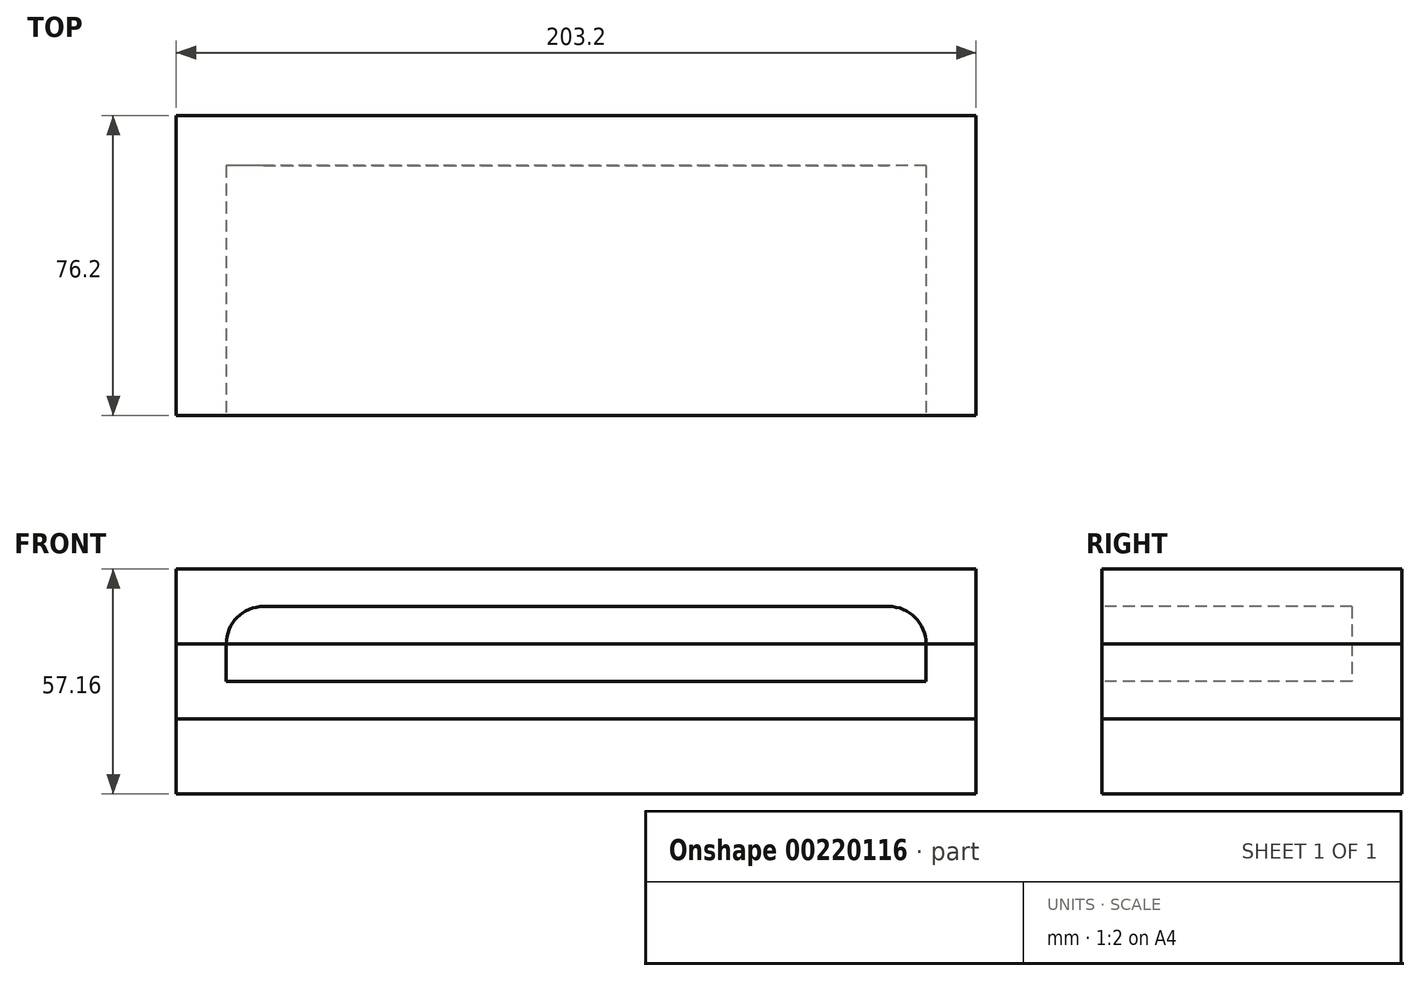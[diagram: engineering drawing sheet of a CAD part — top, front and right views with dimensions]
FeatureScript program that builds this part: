
annotation { "Feature Type Name" : "Feature", "Feature Type Description" : "" }
export const myFeature = defineFeature(function(context is Context, id is Id, definition is map)
    precondition{}
    {
        {
            assignVariable(context, id + "F0", {"name" : "d", "anyValue" : 76.2 * mm});
        }
        {
            assignVariable(context, id + "F1", {"name" : "top_th", "anyValue" : 3 / 101.6 * mm});
        }
        {
            assignVariable(context, id + "F2", {"name" : "bot_th", "anyValue" : getVariable(context, 'top_th')});
        }
        {
            assignVariable(context, id + "F3", {"name" : "slit_d", "anyValue" : 63.5 * mm});
        }
        {
            assignVariable(context, id + "F4", {"name" : "chamfer_angle", "anyValue" : 7});
        }
        {
            var Q0;
            Q0=qCreatedBy(makeId("Front.planeOp"),FACE);
            var sketch = newSketch(context, id + "F5", { "sketchPlane" : qUnion([Q0])});
            skLineSegment(sketch, "E0.bottom", {"start": v(-101.6, 9.52) * mm, "end": v(101.6, 9.52) * mm});
            skLineSegment(sketch, "E0.top", {"start": v(-101.6, -9.53) * mm, "end": v(101.6, -9.53) * mm});
            skLineSegment(sketch, "E0.left", {"start": v(-101.6, 9.52) * mm, "end": v(-101.6, -9.53) * mm});
            skLineSegment(sketch, "E0.right", {"start": v(101.6, 9.52) * mm, "end": v(101.6, -9.53) * mm});
            skSolve(sketch);
        }
        {
            var Q0;
            Q0=makeQuery(id+"F5.imprint","IMPRINT",FACE,{"disambiguationData":[TD([[makeQuery(id+"F5.imprint","IMPRINT",EDGE,{"derivedFrom":sQuery(id+"F5.wireOp",EDGE,"E0.bottom")}),-1.0]])]});
            var sketch = newSketch(context, id + "F6", { "sketchPlane" : qUnion([Q0])});
            skLineSegment(sketch, "E1.bottom", {"start": v(101.6, -9.52) * mm, "end": v(-101.6, -9.53) * mm});
            skLineSegment(sketch, "E1.top", {"start": v(101.6, -28.57) * mm, "end": v(-101.6, -28.58) * mm});
            skLineSegment(sketch, "E1.left", {"start": v(101.6, -9.52) * mm, "end": v(101.6, -28.57) * mm});
            skLineSegment(sketch, "E1.right", {"start": v(-101.6, -9.53) * mm, "end": v(-101.6, -28.58) * mm});
            skPoint(sketch, "E1.middle", {"position": v(0, -19.05) * mm});
            skSolve(sketch);
        }
        {
            var Q0;
            Q0=makeQuery(id+"F5.imprint","IMPRINT",FACE,{"disambiguationData":[TD([[makeQuery(id+"F5.imprint","IMPRINT",EDGE,{"derivedFrom":sQuery(id+"F5.wireOp",EDGE,"E0.bottom")}),-1.0]])]});
            var sketch = newSketch(context, id + "F7", { "sketchPlane" : qUnion([Q0])});
            skLineSegment(sketch, "E2.bottom", {"start": v(101.6, 9.53) * mm, "end": v(-101.6, 9.52) * mm});
            skLineSegment(sketch, "E2.top", {"start": v(101.6, 28.57) * mm, "end": v(-101.6, 28.57) * mm});
            skLineSegment(sketch, "E2.left", {"start": v(101.6, 9.53) * mm, "end": v(101.6, 28.57) * mm});
            skLineSegment(sketch, "E2.right", {"start": v(-101.6, 9.52) * mm, "end": v(-101.6, 28.57) * mm});
            skPoint(sketch, "E2.middle", {"position": v(0, 19.05) * mm});
            skSolve(sketch);
        }
        {
            var Q0;
            Q0=makeQuery(id+"F7.imprint","IMPRINT",FACE,{"disambiguationData":[TD([[makeQuery(id+"F7.imprint","IMPRINT",EDGE,{"derivedFrom":sQuery(id+"F7.wireOp",EDGE,"E2.bottom")}),1.0]])]});
            extrude(context, id + "F8", {"entities" : qUnion([Q0]), "oppositeDirection" : true, "depth" : getVariable(context, 'd')});
        }
        {
            var Q0;
            Q0=makeQuery(id+"F6.imprint","IMPRINT",FACE,{"disambiguationData":[TD([[makeQuery(id+"F6.imprint","IMPRINT",EDGE,{"derivedFrom":sQuery(id+"F6.wireOp",EDGE,"E1.bottom")}),1.0]])]});
            extrude(context, id + "F9", {"entities" : qUnion([Q0]), "oppositeDirection" : true, "depth" : getVariable(context, 'd')});
        }
        {
            var Q0;
            Q0=makeQuery(id+"F6.imprint","IMPRINT",FACE,{"disambiguationData":[TD([[makeQuery(id+"F6.imprint","IMPRINT",EDGE,{"derivedFrom":sQuery(id+"F6.wireOp",EDGE,"E1.bottom")}),-1.0]])]});
            extrude(context, id + "F10", {"entities" : qUnion([Q0]), "oppositeDirection" : true, "depth" : getVariable(context, 'd')});
        }
        {
            var Q0;
            Q0=makeQuery(id+"F7.imprint","IMPRINT",FACE,{"disambiguationData":[TD([[makeQuery(id+"F7.imprint","IMPRINT",EDGE,{"derivedFrom":sQuery(id+"F7.wireOp",EDGE,"E2.bottom")}),-1.0]])]});
            var sketch = newSketch(context, id + "F11", { "sketchPlane" : qUnion([Q0])});
            skLineSegment(sketch, "E3", {"start": v(-79.38, 19.05) * mm, "end": v(79.38, 19.05) * mm});
            skLineSegment(sketch, "E4", {"start": v(-88.9, 9.52) * mm, "end": v(-88.9, 0) * mm});
            skLineSegment(sketch, "E5", {"start": v(-88.9, 0) * mm, "end": v(88.9, 0) * mm});
            skLineSegment(sketch, "E6", {"start": v(88.9, 0) * mm, "end": v(88.9, 9.53) * mm});
            skArc(sketch, "E7", {"start": v(-79.38, 19.05) * mm, "mid": v(-86.11, 16.26) * mm, "end": v(-88.9, 9.52) * mm});
            skArc(sketch, "E8", {"start": v(79.38, 19.05) * mm, "mid": v(86.11, 16.26) * mm, "end": v(88.9, 9.53) * mm});
            skSolve(sketch);
        }
        {
            var Q0;
            Q0 = qSketchRegion(id + "F11", true);
            extrude(context, id + "F12", {"entities" : qUnion([Q0]), "operationType" : NewBodyOperationType.REMOVE, "oppositeDirection" : true, "depth" : getVariable(context, 'slit_d')});
        }
        {
            var Q0;
            Q0=makeQuery(id+"F8.opExtrude","SWEPT_EDGE",EDGE,{"disambiguationData":[OSD([sQuery(id+"F7.wireOp",EDGE,"E2.top"),sQuery(id+"F7.wireOp",EDGE,"E2.right")])]});
            var Q1;
            Q1=makeQuery(id+"F8.opExtrude","SWEPT_EDGE",EDGE,{"disambiguationData":[OSD([sQuery(id+"F7.wireOp",EDGE,"E2.top"),sQuery(id+"F7.wireOp",EDGE,"E2.left")])]});
            var Q2;
            Q2=makeQuery(id+"F8.opExtrude","CAP_EDGE",EDGE,{"disambiguationData":[OSD([sQuery(id+"F7.wireOp",EDGE,"E2.top")])],"isStart":false});
            var Q3;
            Q3=makeQuery(id+"F8.opExtrude","CAP_EDGE",EDGE,{"disambiguationData":[OSD([sQuery(id+"F7.wireOp",EDGE,"E2.top")])],"isStart":true});
            chamfer(context, id + "F13", {"entities" : qUnion([Q0, Q1, Q2, Q3]), "chamferType" : ChamferType.OFFSET_ANGLE, "width" : getVariable(context, 'top_th'), "oppositeDirection" : true, "angle" : (getVariable(context, 'chamfer_angle')) * degree, "tangentPropagation" : true});
        }
        {
            var Q0;
            Q0=makeQuery(id+"F10.opExtrude","SWEPT_FACE",FACE,{"disambiguationData":[OSD([sQuery(id+"F6.wireOp",EDGE,"E1.top")])]});
            chamfer(context, id + "F14", {"entities" : qUnion([Q0]), "chamferType" : ChamferType.OFFSET_ANGLE, "width" : getVariable(context, 'bot_th'), "oppositeDirection" : true, "angle" : (getVariable(context, 'chamfer_angle')) * degree, "tangentPropagation" : true});
        }
    });
